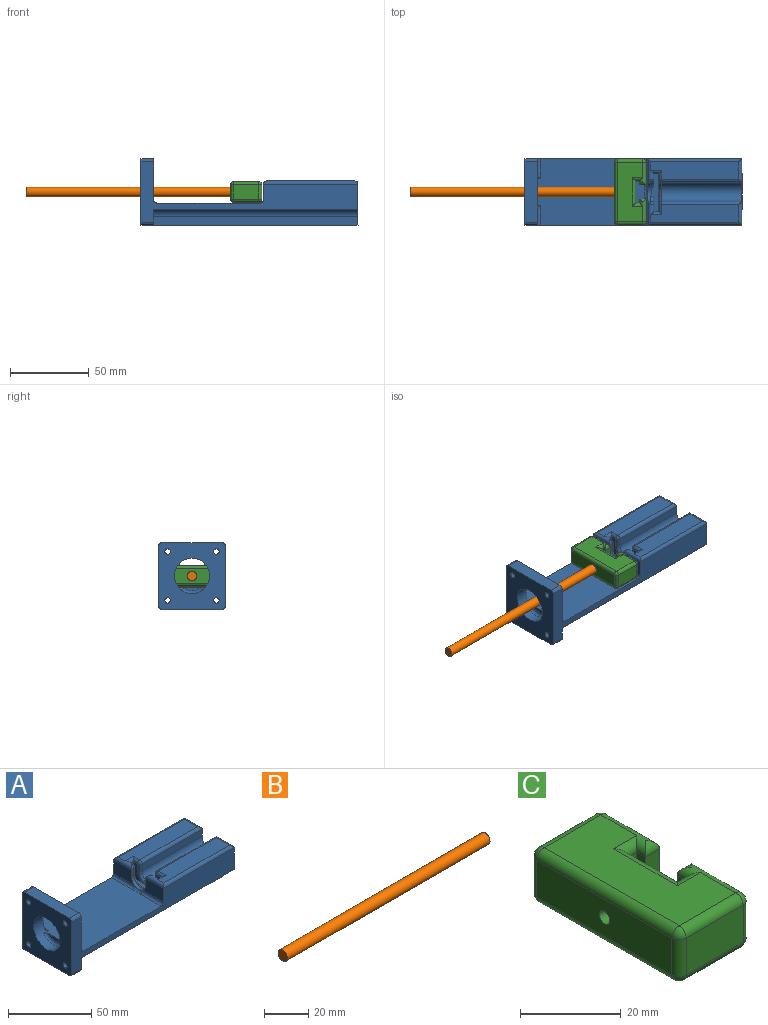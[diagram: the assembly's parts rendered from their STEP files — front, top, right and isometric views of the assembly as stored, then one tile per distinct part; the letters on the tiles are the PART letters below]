
ASSEMBLY  parts=3 mates=2
PART A: 77 faces, bbox 138.9x43.2x43.2 mm
  f0: plane 17.83x10mm, normal (-1,0,0), area 155.5mm2, adj f10,f11,f18,f44,f76
  f1: plane 12x8.59mm, normal (1,0,0), area 61.8mm2, adj f40,f52,f53,f54,f55
  f2: plane 12x8.59mm, normal (-1,0,0), area 61.8mm2, adj f52,f53,f61,f64,f66
  f3: plane 56x11.15mm, normal (0,0,1), area 585.5mm2, adj f9,f41,f42,f44,f65,f67
  f4: plane 56x11.15mm, normal (0,0,1), area 579.2mm2, adj f8,f37,f39,f40,f59,f61
  f5: plane 51x5mm, normal (0,-1,0), area 255mm2, adj f6,f9,f33,f71
  f6: cylinder r=6mm len=51mm, axis (-1,0,0), area 961.3mm2, adj f5,f7,f33,f66,f68,f70
  f7: plane 51x5mm, normal (0,1,0), area 255mm2, adj f6,f8,f33,f64
  f8: cylinder r=2mm len=51mm, axis (1,0,0), area 157.1mm2, adj f4,f7,f37,f63
  f9: cylinder r=2mm len=51mm, axis (-1,0,0), area 157.1mm2, adj f3,f5,f41,f69
  f10: plane 5x2mm, normal (0,-1,0), area 10mm2, adj f0,f11,f43,f60
  f11: cylinder r=6mm len=12mm, axis (-1,0,0), area 37.7mm2, adj f0,f10,f12,f34,f55,f57,f58,f75
  f12: plane 5x2mm, normal (0,1,0), area 10mm2, adj f11,f34,f38,f54
  f13: plane 12.09x2.25mm, normal (-1,0,0), area 18.6mm2, adj f35,f36
  f14: plane 42.3x26.15mm, normal (1,0,0), area 777.7mm2, adj f16,f18,f20,f21,f22,f23,f47,f48
  f15: plane 10.15x10.15mm, normal (1,0,0), area 88.2mm2, adj f16,f17,f24,f27,f31,f32,f45
  f16: plane 138x38.3mm, normal (0,-1,0), area 1548.2mm2, adj f14,f15,f26,f31,f33,f34,f35,f39
  f17: plane 138x38.3mm, normal (0,0,-1), area 3271.4mm2, adj f15,f25,f26,f27,f28,f33,f45,f46
  f18: plane 138x38.3mm, normal (0,1,0), area 1651.9mm2, adj f0,f14,f25,f26,f30,f33,f35,f42
  f19: cylinder r=1.75mm len=8mm, axis (-1,0,0), area 88mm2, adj f25,f26
  f20: cylinder r=1.75mm len=8mm, axis (-1,0,0), area 88mm2, adj f14,f26
  f21: cylinder r=1.75mm len=8mm, axis (-1,0,0), area 88mm2, adj f14,f26
  f22: cylinder r=11.25mm len=22.5mm, axis (-1,0,0), area 529.8mm2, adj f14,f26,f35,f36,f72,f73
  f23: plane 38.3x8mm, normal (0,0,1), area 306.4mm2, adj f14,f26,f47,f48
  f24: cylinder r=1.75mm len=8mm, axis (-1,0,0), area 88mm2, adj f15,f26
  f25: plane 9.35x9.35mm, normal (1,0,0), area 74mm2, adj f17,f18,f19,f28,f29,f30,f46
  f26: plane 42.3x42.3mm, normal (-1,0,0), area 1349.8mm2, adj f16,f17,f18,f19,f20,f21,f22,f23
  f27: plane 130x5.79mm, normal (0,-1,0), area 752.7mm2, adj f15,f17,f32,f33
  f28: plane 130x5.41mm, normal (0,1,0), area 703.5mm2, adj f17,f25,f29,f33
  f29: cylinder r=3.7mm len=130mm, axis (-1,0,0), area 787mm2, adj f25,f28,f30,f33
  f30: plane 130x5.65mm, normal (0,0,-1), area 734.5mm2, adj f18,f25,f29,f33
  f31: plane 130x5.71mm, normal (0,0,-1), area 742.1mm2, adj f15,f16,f32,f33
  f32: cylinder r=4.5mm len=130mm, axis (-1,0,0), area 893.1mm2, adj f15,f27,f31,f33
  f33: plane 42.3x26.15mm, normal (1,0,0), area 806.5mm2, adj f5,f6,f7,f16,f17,f18,f27,f28
  f34: plane 17.83x10mm, normal (-1,0,0), area 155.5mm2, adj f11,f12,f16,f40,f74
  f35: plane 71.16x43.19mm, normal (0,0,1), area 2830.2mm2, adj f13,f16,f18,f22,f36,f72,f73,f74
  f36: torus R=9.25mm, axis (1,0,0), area 53.5mm2, adj f13,f22,f35
  f37: cylinder r=2mm len=15.15mm, axis (0,1,0), area 41.3mm2, adj f4,f8,f33,f39
  f38: cylinder r=2mm len=2mm, axis (1,0,0), area 3.1mm2, adj f12,f40,f56
  f39: cylinder r=2mm len=60mm, axis (-1,0,0), area 182.2mm2, adj f4,f16,f37,f40
  f40: cylinder r=2mm len=15.15mm, axis (0,-1,0), area 58.5mm2, adj f1,f4,f34,f38,f39,f56,f59
  f41: cylinder r=2mm len=15.15mm, axis (0,1,0), area 41.3mm2, adj f3,f9,f33,f42
  f42: cylinder r=2mm len=60mm, axis (1,0,0), area 182.2mm2, adj f3,f18,f41,f44
  f43: cylinder r=2mm len=2mm, axis (-1,0,0), area 3.1mm2, adj f10,f44,f62
  f44: cylinder r=2mm len=15.15mm, axis (0,-1,0), area 55.6mm2, adj f0,f3,f42,f43,f51,f62,f65
  f45: cylinder r=2mm len=8mm, axis (1,0,0), area 25.1mm2, adj f15,f16,f17,f26
  f46: cylinder r=2mm len=8mm, axis (-1,0,0), area 25.1mm2, adj f17,f18,f25,f26
  f47: cylinder r=2mm len=8mm, axis (1,0,0), area 25.1mm2, adj f14,f18,f23,f26
  f48: cylinder r=2mm len=8mm, axis (-1,0,0), area 25.1mm2, adj f14,f16,f23,f26
  f49: plane 12x7.69mm, normal (-1,0,0), area 51.1mm2, adj f50,f53,f67,f70,f71
  f50: plane 12x3mm, normal (0,-1,0), area 36mm2, adj f49,f51,f53,f65
  f51: plane 12x7.69mm, normal (1,0,0), area 51.1mm2, adj f44,f50,f53,f58,f60
  f52: plane 12x3mm, normal (0,1,0), area 36mm2, adj f1,f2,f53,f59
  f53: plane 24.15x3.13mm, normal (0,0,1), area 72.1mm2, adj f1,f2,f49,f50,f51,f52,f57,f68
  f54: cylinder r=2mm len=5mm, axis (0,0,-1), area 15.7mm2, adj f1,f12,f55,f56
  f55: torus R=8mm, axis (-1,0,0), area 22.5mm2, adj f1,f11,f54,f57
  f56: sphere r=2mm, area 6.3mm2, adj f38,f40,f54
  f57: bspline ~8.83x2.38mm, area 16mm2, adj f11,f53,f55,f58
  f58: torus R=8mm, axis (-1,0,0), area 22.5mm2, adj f11,f51,f57,f60
  f59: cylinder r=2mm len=7mm, axis (-1,0,0), area 15.7mm2, adj f4,f40,f52,f61
  f60: cylinder r=2mm len=5mm, axis (0,0,1), area 15.7mm2, adj f10,f51,f58,f62
  f61: cylinder r=2mm len=6.46mm, axis (0,-1,0), area 17.1mm2, adj f2,f4,f59,f63
  f62: sphere r=2mm, area 6.3mm2, adj f43,f44,f60
  f63: sphere r=2mm, area 6.3mm2, adj f8,f61,f64
  f64: cylinder r=2mm len=5mm, axis (0,0,1), area 15.7mm2, adj f2,f7,f63,f66
  f65: cylinder r=2mm len=7mm, axis (1,0,0), area 15.7mm2, adj f3,f44,f50,f67
  f66: torus R=8mm, axis (-1,0,0), area 22.5mm2, adj f2,f6,f64,f68
  f67: cylinder r=2mm len=5.56mm, axis (0,-1,0), area 14.3mm2, adj f3,f49,f65,f69
  f68: bspline ~8.83x2.38mm, area 16mm2, adj f6,f53,f66,f70
  f69: sphere r=2mm, area 6.3mm2, adj f9,f67,f71
  f70: torus R=8mm, axis (-1,0,0), area 22.5mm2, adj f6,f49,f68,f71
  f71: cylinder r=2mm len=5mm, axis (0,0,-1), area 15.7mm2, adj f5,f49,f69,f70
  f72: cylinder r=2mm len=12.34mm, axis (0,-1,0), area 36.8mm2, adj f14,f16,f22,f35
  f73: cylinder r=2mm len=12.34mm, axis (0,-1,0), area 36.8mm2, adj f14,f18,f22,f35
  f74: cylinder r=2mm len=17.83mm, axis (0,-1,0), area 56mm2, adj f16,f34,f35,f75
  f75: bspline ~6.63x2mm, area 16.3mm2, adj f11,f35,f74,f76
  f76: cylinder r=2mm len=17.83mm, axis (0,-1,0), area 56mm2, adj f0,f18,f35,f75
PART B: 3 faces, bbox 130x6x6 mm
  f0: cylinder r=3mm len=130mm, axis (-1,0,0), area 2450.4mm2, adj f1,f2
  f1: plane 6x6mm, normal (1,0,0), area 28.3mm2, adj f0
  f2: plane 6x6mm, normal (-1,0,0), area 28.3mm2, adj f0
PART C: 42 faces, bbox 20x42x13 mm
  f0: plane 14x11mm, normal (1,0,0), area 146.9mm2, adj f1,f11,f13,f14,f21
  f1: plane 11x2.5mm, normal (0,-1,0), area 27.5mm2, adj f0,f2,f13,f19
  f2: plane 11x2.5mm, normal (-1,0,0), area 27.5mm2, adj f1,f3,f13,f15
  f3: plane 11x4mm, normal (0,-1,0), area 43.1mm2, adj f2,f4,f13,f16,f33
  f4: plane 14.5x9mm, normal (1,0,0), area 130.5mm2, adj f3,f15,f25,f33
  f5: plane 16x9mm, normal (0,1,0), area 144mm2, adj f17,f25,f27,f35
  f6: plane 38x9mm, normal (-1,0,0), area 334.9mm2, adj f14,f18,f27,f29,f37
  f7: plane 16x9mm, normal (0,-1,0), area 144mm2, adj f20,f29,f31,f39
  f8: plane 14.5x9mm, normal (1,0,0), area 130.5mm2, adj f9,f22,f31,f41
  f9: plane 11x4mm, normal (0,1,0), area 43.1mm2, adj f8,f10,f13,f24,f41
  f10: plane 11x2.5mm, normal (-1,0,0), area 27.5mm2, adj f9,f11,f13,f22
  f11: plane 11x2.5mm, normal (0,1,0), area 27.5mm2, adj f0,f10,f13,f23
  f12: plane 38x16mm, normal (0,0,1), area 491mm2, adj f15,f17,f18,f19,f20,f21,f22,f23
  f13: plane 38x16mm, normal (0,0,-1), area 555mm2, adj f0,f1,f2,f3,f9,f10,f11,f33
  f14: cylinder r=1.5mm len=13.5mm, axis (-1,0,0), area 127.2mm2, adj f0,f6
  f15: cylinder r=2mm len=14.5mm, axis (0,-1,0), area 51.1mm2, adj f2,f4,f12,f16,f19,f26
  f16: cylinder r=2mm len=4mm, axis (-1,0,0), area 8mm2, adj f3,f15
  f17: cylinder r=2mm len=16mm, axis (1,0,0), area 50.3mm2, adj f5,f12,f26,f28
  f18: cylinder r=2mm len=38mm, axis (0,1,0), area 119.4mm2, adj f6,f12,f28,f30
  f19: cylinder r=2mm len=6.5mm, axis (-1,0,0), area 12.4mm2, adj f1,f12,f15,f21
  f20: cylinder r=2mm len=16mm, axis (-1,0,0), area 50.3mm2, adj f7,f12,f30,f32
  f21: cylinder r=2mm len=18mm, axis (0,-1,0), area 48.5mm2, adj f0,f12,f19,f23
  f22: cylinder r=2mm len=14.5mm, axis (0,-1,0), area 51.1mm2, adj f8,f10,f12,f23,f24,f32
  f23: cylinder r=2mm len=6.5mm, axis (1,0,0), area 12.4mm2, adj f11,f12,f21,f22
  f24: cylinder r=2mm len=4mm, axis (1,0,0), area 8mm2, adj f9,f22
  f25: cylinder r=2mm len=9mm, axis (0,0,-1), area 28.3mm2, adj f4,f5,f26,f34
  f26: sphere r=2mm, area 6.3mm2, adj f15,f17,f25
  f27: cylinder r=2mm len=9mm, axis (0,0,1), area 28.3mm2, adj f5,f6,f28,f36
  f28: sphere r=2mm, area 6.3mm2, adj f17,f18,f27
  f29: cylinder r=2mm len=9mm, axis (0,0,-1), area 28.3mm2, adj f6,f7,f30,f38
  f30: sphere r=2mm, area 6.3mm2, adj f18,f20,f29
  f31: cylinder r=2mm len=9mm, axis (0,0,1), area 28.3mm2, adj f7,f8,f32,f40
  f32: sphere r=2mm, area 6.3mm2, adj f20,f22,f31
  f33: cylinder r=2mm len=14.5mm, axis (0,1,0), area 45.6mm2, adj f3,f4,f13,f34
  f34: sphere r=2mm, area 6.3mm2, adj f25,f33,f35
  f35: cylinder r=2mm len=16mm, axis (-1,0,0), area 50.3mm2, adj f5,f13,f34,f36
  f36: sphere r=2mm, area 6.3mm2, adj f27,f35,f37
  f37: cylinder r=2mm len=38mm, axis (0,-1,0), area 119.4mm2, adj f6,f13,f36,f38
  f38: sphere r=2mm, area 6.3mm2, adj f29,f37,f39
  f39: cylinder r=2mm len=16mm, axis (1,0,0), area 50.3mm2, adj f7,f13,f38,f40
  f40: sphere r=2mm, area 6.3mm2, adj f31,f39,f41
  f41: cylinder r=2mm len=14.5mm, axis (0,1,0), area 45.6mm2, adj f8,f9,f13,f40
PLACE A t=(-67.94,0.24,0.2)mm fixed
PLACE B t=(-141.03,0.24,0.2)mm
PLACE C t=(-1.03,0.24,0.2)mm
MATE slider A.f22 <-> B.f0  axis (-1,0,0) through (-67.94,0.24,0.2)mm
MATE fastened C.f14 <-> B.f0  axis (-1,0,0) through (-11.03,0.24,0.2)mm
